# Revit family: РОСМА_МанометрКоррозионностойкийВиброустойчивый_160МПа
name_source: partatom
category: Арматура трубопроводов
revit_build: Autodesk Revit 2018 (Build: 20180423_1000(x64)
units: mm (PartAtom-declared; Revit-internal decimal feet)

## family parameters
Всегда вертикально = Да
На основе рабочей плоскости = Нет
Общий = Нет
При загрузке вырезать с полостями = Нет
Размер круглого соединителя = Использовать диаметр
Тип детали = Вставляется

## types (2) — shared parameters
ADSK_Единица измерения = шт.
ADSK_Количество = 1
DN = 15.00 мм
Ddempfer = 6 мм
Table = спец_коррозионностойкий виброустойчивый до 160МПа
Table_2 = размеры_коррозионностойкий виброустойчивый до 160МПа
URL = https://rosma.spb.ru
Группа модели = Оборудование
Изготовитель = ЗАО "РОСМА"
Класс точности = 1,0
Климатическое исполнение = Группа Д2 по ГОСТ Р 52931; климатическое исполнение УХЛ категории 1.1 по ГОСТ 15150
Код IP = IP65
Межповерочный интервал = 2 года
Описание = Тип ТМ, серия 21. Промышленные манометры, устойчивые к воздействию агрессивных измеряемых сред, с возможностью гидрозаполнения (виброустойчивый).
Радиальное присоединение = Да
Счетчик списка = 26
Техническая документация = ТУ 4212-001-4719015564-2008; ГОСТ 2405–88
лого_задн_стенка = Да

## per-type parameters (varying)
| type | Объем заполняемой жидкости |
| 621 | 1000 мл |
| 521 | 350 мл |

note: column(s) folded — value = type name in every type: Исполнение
